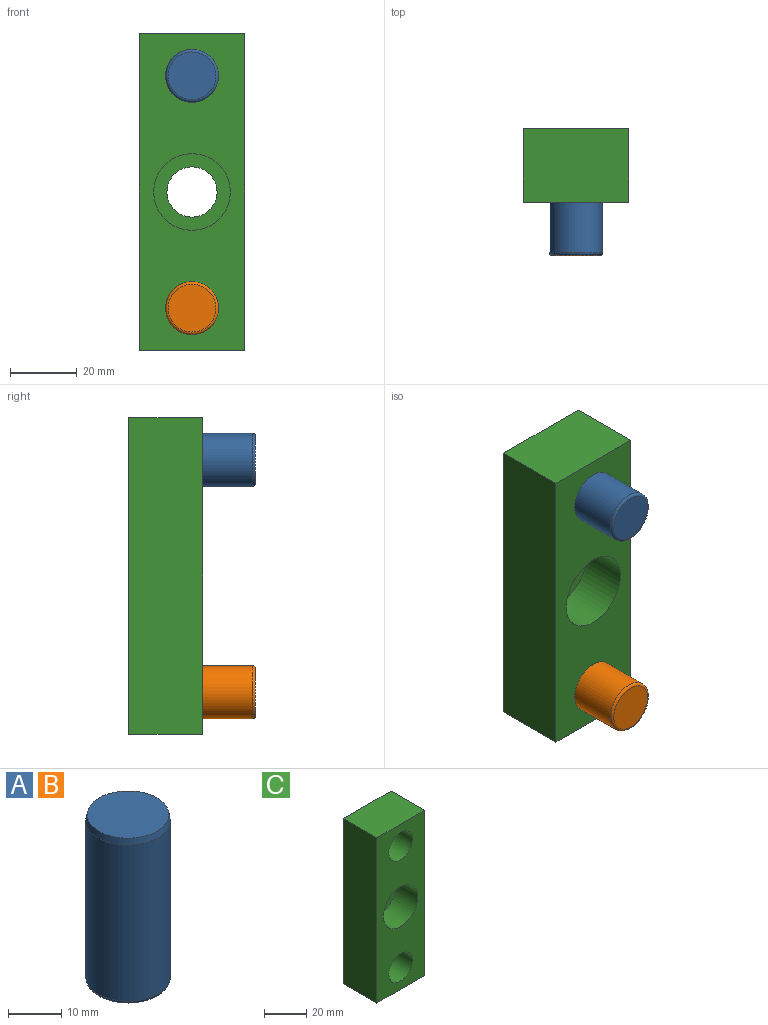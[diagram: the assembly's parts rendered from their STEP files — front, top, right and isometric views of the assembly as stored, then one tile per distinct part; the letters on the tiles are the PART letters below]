
ASSEMBLY  parts=3 mates=2
PART A: 5 faces, bbox 17.2x17.2x38.1 mm
  f0: cylinder r=7.94mm len=35.9mm, axis (0,0,-1), area 1790.3mm2, adj f3,f4
  f1: plane 15.37x15.37mm, normal (0,0,1), area 185.5mm2, adj f3
  f2: plane 14.35x14.35mm, normal (0,0,-1), area 161.8mm2, adj f4
  f3: cone r=7.68mm half-angle=10deg, axis (0,0,-1), area 71.8mm2, adj f0,f1
  f4: torus R=7.18mm, axis (0,0,1), area 57.6mm2, adj f0,f2
PART B: same geometry as A
PART C: 11 faces, bbox 31.8x22.2x95.3 mm
  f0: plane 31.75x22.23mm, normal (0,0,-1), area 705.6mm2, adj f1,f3,f4,f5
  f1: plane 95.25x22.23mm, normal (1,0,0), area 2116.9mm2, adj f0,f2,f4,f5
  f2: plane 31.75x22.23mm, normal (0,0,1), area 705.6mm2, adj f1,f3,f4,f5
  f3: plane 95.25x22.23mm, normal (-1,0,0), area 2116.9mm2, adj f0,f2,f4,f5
  f4: plane 95.25x31.75mm, normal (0,-1,0), area 2212.2mm2, adj f0,f1,f2,f3,f8,f9,f10
  f5: plane 95.25x31.75mm, normal (0,1,0), area 2449.7mm2, adj f0,f1,f2,f3,f6,f9,f10
  f6: cylinder r=7.54mm len=15.08mm, axis (0,-1,0), area 376.1mm2, adj f5,f7
  f7: plane 23.02x23.02mm, normal (0,-1,0), area 237.5mm2, adj f6,f8
  f8: cylinder r=11.51mm len=23.02mm, axis (0,-1,0), area 1033.2mm2, adj f4,f7
  f9: cylinder r=7.94mm len=22.23mm, axis (0,-1,0), area 1108.4mm2, adj f4,f5
  f10: cylinder r=7.94mm len=22.23mm, axis (0,-1,0), area 1108.4mm2, adj f4,f5
PLACE A rot(axis=(-1,0,0),90deg) t=(-56.42,-32.25,75.89)mm
PLACE B rot(axis=(-1,0,0),90deg) t=(-56.42,-32.25,6.04)mm
PLACE C t=(-40.55,5.85,-6.66)mm
MATE fastened B.f0 <-> C.f9  axis (0,1,0) through (-56.42,5.85,6.04)mm
MATE fastened A.f0 <-> C.f10  axis (0,1,0) through (-56.42,5.85,75.89)mm
